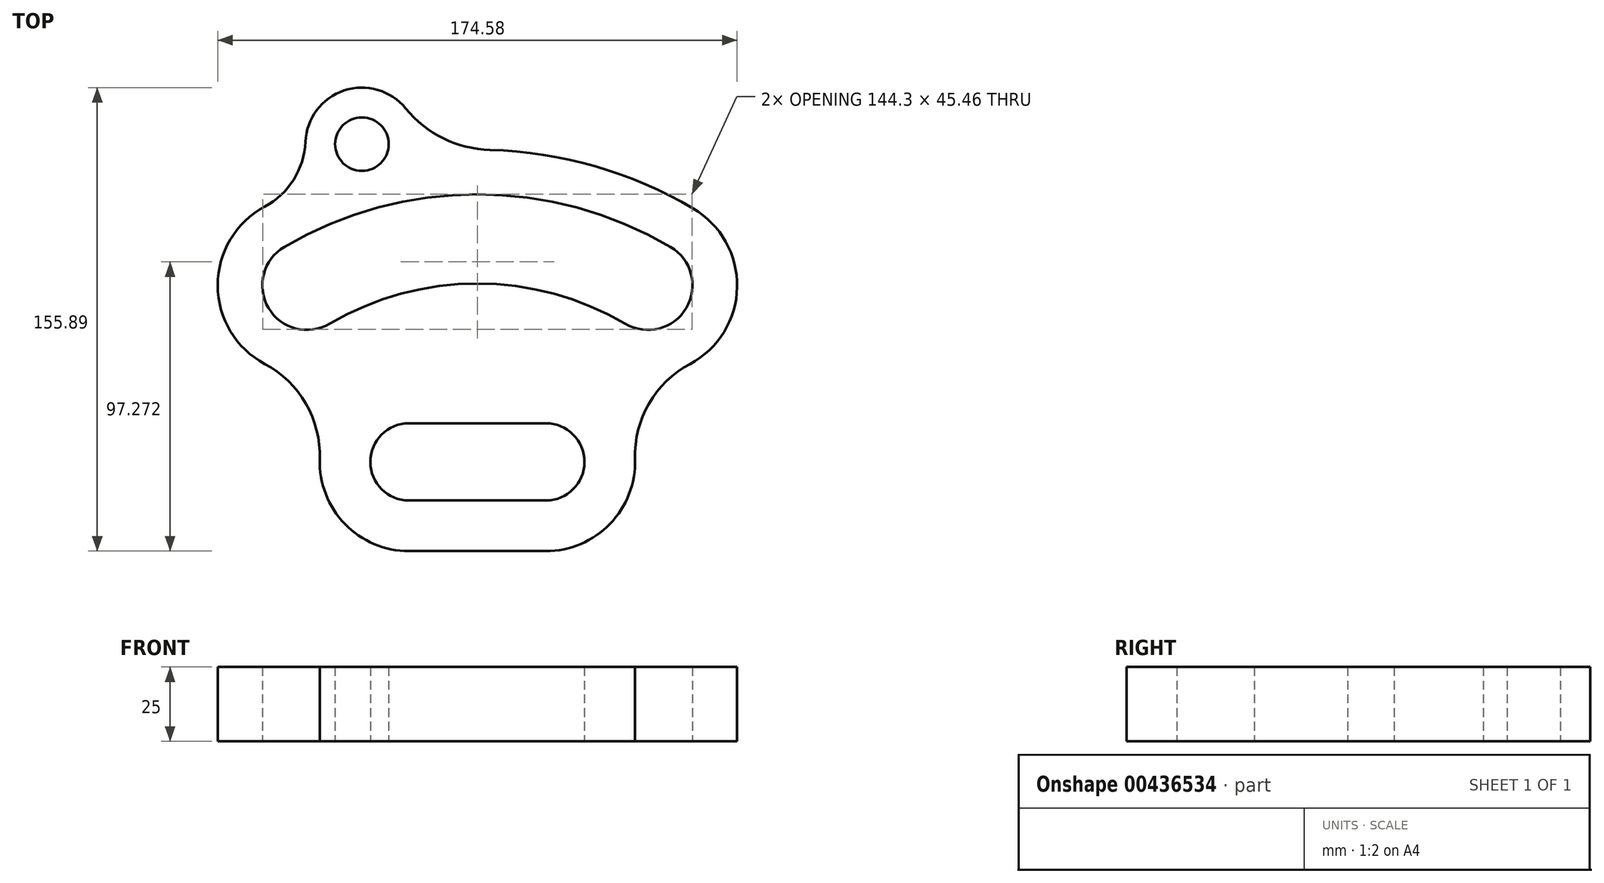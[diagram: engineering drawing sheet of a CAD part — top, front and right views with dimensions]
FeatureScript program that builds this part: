
annotation { "Feature Type Name" : "Feature", "Feature Type Description" : "" }
export const myFeature = defineFeature(function(context is Context, id is Id, definition is map)
    precondition{}
    {
        {
            var Q0;
            Q0=qCreatedBy(makeId("Top.planeOp"),FACE);
            var sketch = newSketch(context, id + "F0", { "sketchPlane" : qUnion([Q0])});
            skArc(sketch, "E0", {"start": v(-57.3, 97.4) * mm, "mid": v(0, 113) * mm, "end": v(57.3, 97.4) * mm, "construction": true});
            skArc(sketch, "E1", {"start": v(-64.9, 110.33) * mm, "mid": v(-70.22, 89.8) * mm, "end": v(-49.69, 84.47) * mm});
            skArc(sketch, "E2", {"start": v(49.69, 84.47) * mm, "mid": v(70.22, 89.8) * mm, "end": v(64.9, 110.33) * mm});
            skLineSegment(sketch, "E3", {"start": v(0, 0) * mm, "end": v(0, 158.54) * mm, "construction": true});
            skLineSegment(sketch, "E4", {"start": v(-47.57, 38) * mm, "end": v(59.67, 38) * mm, "construction": true});
            skArc(sketch, "E5", {"start": v(23, 51) * mm, "mid": v(36, 38) * mm, "end": v(23, 25) * mm});
            skArc(sketch, "E6", {"start": v(-23, 51) * mm, "mid": v(-36, 38) * mm, "end": v(-23, 25) * mm});
            skLineSegment(sketch, "E7", {"start": v(-23, 25) * mm, "end": v(23, 25) * mm});
            skLineSegment(sketch, "E8", {"start": v(-23, 51) * mm, "end": v(23, 51) * mm});
            skLineSegment(sketch, "E9", {"start": v(-23, 51) * mm, "end": v(-23, 25) * mm, "construction": true});
            skLineSegment(sketch, "E10", {"start": v(23, 51) * mm, "end": v(23, 25) * mm, "construction": true});
            skLineSegment(sketch, "E11", {"start": v(-23, 38) * mm, "end": v(-67.79, 115.57) * mm, "construction": true});
            skLineSegment(sketch, "E12", {"start": v(23, 38) * mm, "end": v(77.68, 132.71) * mm, "construction": true});
            skArc(sketch, "E13", {"start": v(-49.69, 84.47) * mm, "mid": v(0, 98) * mm, "end": v(49.69, 84.47) * mm});
            skArc(sketch, "E14", {"start": v(-64.9, 110.33) * mm, "mid": v(0, 128) * mm, "end": v(64.9, 110.33) * mm});
            skArc(sketch, "E15", {"start": v(-80.46, 126.6) * mm, "mid": v(-69.95, 132.7) * mm, "end": v(-58.98, 137.92) * mm, "construction": true});
            skLineSegment(sketch, "E16", {"start": v(0, 0) * mm, "end": v(-45.4, 169.47) * mm, "construction": true});
            skCircle(sketch, "E17", {"center": v(-38.82, 144.89) * mm, "radius": 9 * mm});
            skArc(sketch, "E18", {"start": v(-57.8, 145.67) * mm, "mid": v(-44.83, 162.91) * mm, "end": v(-24.1, 156.9) * mm});
            skArc(sketch, "E19", {"start": v(4.22, 142.94) * mm, "mid": v(39.6, 137.4) * mm, "end": v(72.5, 123.26) * mm});
            skArc(sketch, "E20", {"start": v(72.5, 123.26) * mm, "mid": v(87.29, 96.8) * mm, "end": v(71.45, 70.95) * mm});
            skPoint(sketch, "E21.visualSharp", {"position": v(-20.11, 141.58) * mm});
            skArc(sketch, "E21.filletArc", {"start": v(-24.1, 156.9) * mm, "mid": v(-11.46, 146.84) * mm, "end": v(4.22, 142.94) * mm});
            skArc(sketch, "E22", {"start": v(-71.49, 123.83) * mm, "mid": v(-87.3, 97.38) * mm, "end": v(-71.45, 70.95) * mm});
            skArc(sketch, "E23", {"start": v(-52.98, 38.96) * mm, "mid": v(-44.55, 17.13) * mm, "end": v(-23, 8) * mm});
            skArc(sketch, "E24", {"start": v(52.98, 38.96) * mm, "mid": v(44.55, 17.13) * mm, "end": v(23, 8) * mm});
            skLineSegment(sketch, "E25", {"start": v(-23, 8) * mm, "end": v(23, 8) * mm});
            skArc(sketch, "E26", {"start": v(71.45, 70.95) * mm, "mid": v(57.66, 57.6) * mm, "end": v(52.98, 38.96) * mm});
            skArc(sketch, "E27", {"start": v(-52.98, 38.96) * mm, "mid": v(-57.66, 57.6) * mm, "end": v(-71.45, 70.95) * mm});
            skArc(sketch, "E28", {"start": v(-71.49, 123.83) * mm, "mid": v(-61.75, 132.94) * mm, "end": v(-57.8, 145.67) * mm});
            skSolve(sketch);
        }
        {
            var Q0;
            Q0=makeQuery(id+"F0.imprint","IMPRINT",FACE,{"disambiguationData":[TD([[makeQuery(id+"F0.imprint","IMPRINT",EDGE,{"derivedFrom":sQuery(id+"F0.wireOp",EDGE,"E1")}),-1.0]])]});
            extrude(context, id + "F1", {"entities" : qUnion([Q0]), "depth" : 25 * mm});
        }
    });
